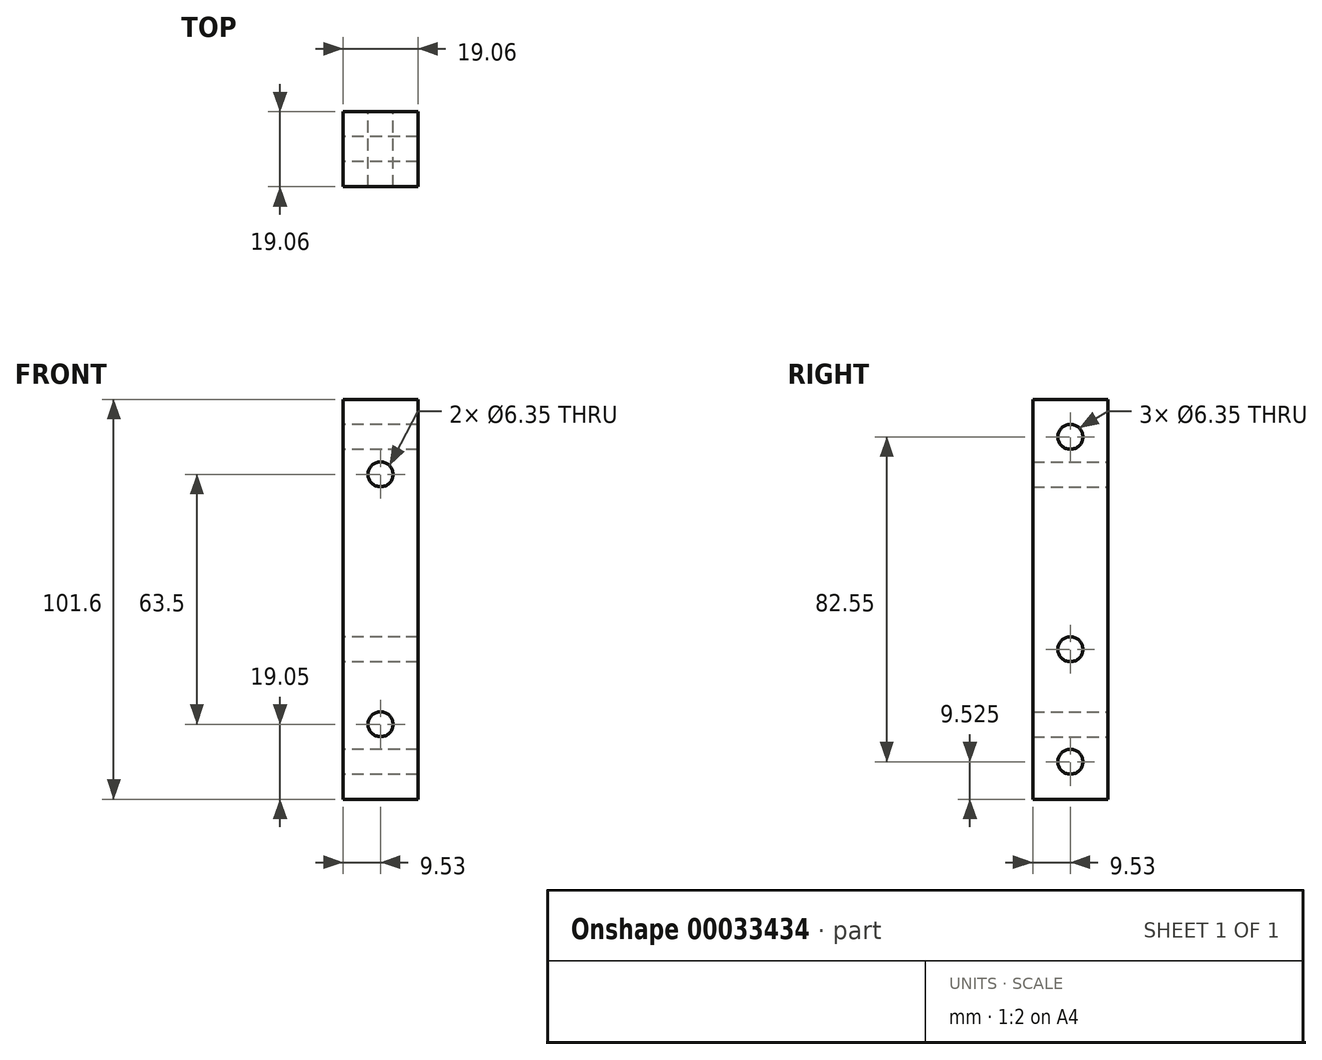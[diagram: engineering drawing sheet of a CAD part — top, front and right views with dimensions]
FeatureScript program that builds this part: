
annotation { "Feature Type Name" : "Feature", "Feature Type Description" : "" }
export const myFeature = defineFeature(function(context is Context, id is Id, definition is map)
    precondition{}
    {
        {
            var Q0;
            Q0=qCreatedBy(makeId("Right.planeOp"),FACE);
            var sketch = newSketch(context, id + "F0", { "sketchPlane" : qUnion([Q0])});
            skLineSegment(sketch, "E0.rect.bottom", {"start": v(-9.52, 50.8) * mm, "end": v(9.53, 50.8) * mm});
            skLineSegment(sketch, "E0.rect.top", {"start": v(-9.52, -50.8) * mm, "end": v(9.52, -50.8) * mm});
            skLineSegment(sketch, "E0.rect.left", {"start": v(-9.52, 50.8) * mm, "end": v(-9.53, -50.8) * mm});
            skLineSegment(sketch, "E0.rect.right", {"start": v(9.53, 50.8) * mm, "end": v(9.52, -50.8) * mm});
            skPoint(sketch, "E0.rect.middle", {"position": v(0, 0) * mm});
            skSolve(sketch);
        }
        {
            var Q0;
            Q0 = qSketchRegion(id + "F0", true);
            extrude(context, id + "F1", {"entities" : qUnion([Q0]), "depth" : 19.05 * mm, "symmetric" : true});
        }
        {
            var Q0;
            Q0=makeQuery(id+"F1.opExtrude","SWEPT_FACE",FACE,{"disambiguationData":[OSD([sQuery(id+"F0.wireOp",EDGE,"E0.rect.left")])]});
            var sketch = newSketch(context, id + "F2", { "sketchPlane" : qUnion([Q0])});
            skLineSegment(sketch, "E1", {"start": v(0, 31.75) * mm, "end": v(0, -31.75) * mm, "construction": true});
            skSolve(sketch);
        }
        {
            var Q0;
            Q0=sQuery(id+"F2.wireOp",VERTEX,"E1.start");
            var Q1;
            Q1=sQuery(id+"F2.wireOp",VERTEX,"E1.end");
            var Q2;
            Q2=makeQuery(id+"F1.opExtrude","SWEPT_BODY",BODY,{"disambiguationData":[OSD([sQuery(id+"F0.wireOp",EDGE,"E0.rect.bottom"),sQuery(id+"F0.wireOp",EDGE,"E0.rect.top"),sQuery(id+"F0.wireOp",EDGE,"E0.rect.left"),sQuery(id+"F0.wireOp",EDGE,"E0.rect.right")])]});
            hole(context, id + "F3", {"style" : HoleStyle.SIMPLE, "holeDiameter" : 6.35 * mm, "endStyle" : HoleEndStyle.THROUGH, "locations" : qUnion([Q0, Q1]), "scope" : qUnion([Q2])});
        }
        {
            var Q0;
            Q0=makeQuery(id+"F1.opExtrude","CAP_FACE",FACE,{"disambiguationData":[OSD([sQuery(id+"F0.wireOp",EDGE,"E0.rect.bottom"),sQuery(id+"F0.wireOp",EDGE,"E0.rect.top"),sQuery(id+"F0.wireOp",EDGE,"E0.rect.left"),sQuery(id+"F0.wireOp",EDGE,"E0.rect.right")])],"isStart":false});
            var sketch = newSketch(context, id + "F4", { "sketchPlane" : qUnion([Q0])});
            skLineSegment(sketch, "E2", {"start": v(0, 41.28) * mm, "end": v(0, -41.28) * mm, "construction": true});
            skSolve(sketch);
        }
        {
            var Q0;
            Q0=sQuery(id+"F4.wireOp",VERTEX,"E2.start");
            var Q1;
            Q1=sQuery(id+"F4.wireOp",VERTEX,"E2.end");
            var Q2;
            Q2=makeQuery(id+"F1.opExtrude","SWEPT_BODY",BODY,{"disambiguationData":[OSD([sQuery(id+"F0.wireOp",EDGE,"E0.rect.bottom"),sQuery(id+"F0.wireOp",EDGE,"E0.rect.top"),sQuery(id+"F0.wireOp",EDGE,"E0.rect.left"),sQuery(id+"F0.wireOp",EDGE,"E0.rect.right")])]});
            hole(context, id + "F5", {"style" : HoleStyle.SIMPLE, "holeDiameter" : 6.35 * mm, "endStyle" : HoleEndStyle.THROUGH, "locations" : qUnion([Q0, Q1]), "scope" : qUnion([Q2])});
        }
        {
            var Q0;
            Q0=makeQuery(id+"F1.opExtrude","CAP_FACE",FACE,{"disambiguationData":[OSD([sQuery(id+"F0.wireOp",EDGE,"E0.rect.bottom"),sQuery(id+"F0.wireOp",EDGE,"E0.rect.top"),sQuery(id+"F0.wireOp",EDGE,"E0.rect.left"),sQuery(id+"F0.wireOp",EDGE,"E0.rect.right")])],"isStart":false});
            var sketch = newSketch(context, id + "F6", { "sketchPlane" : qUnion([Q0])});
            skLineSegment(sketch, "E3", {"start": v(0, 0) * mm, "end": v(0, -12.7) * mm, "construction": true});
            skSolve(sketch);
        }
        {
            var Q0;
            Q0=sQuery(id+"F6.wireOp",VERTEX,"E3.end");
            var Q1;
            Q1=makeQuery(id+"F1.opExtrude","SWEPT_BODY",BODY,{"disambiguationData":[OSD([sQuery(id+"F0.wireOp",EDGE,"E0.rect.bottom"),sQuery(id+"F0.wireOp",EDGE,"E0.rect.top"),sQuery(id+"F0.wireOp",EDGE,"E0.rect.left"),sQuery(id+"F0.wireOp",EDGE,"E0.rect.right")])]});
            hole(context, id + "F7", {"style" : HoleStyle.SIMPLE, "holeDiameter" : 6.35 * mm, "endStyle" : HoleEndStyle.THROUGH, "locations" : qUnion([Q0]), "scope" : qUnion([Q1])});
        }
    });
